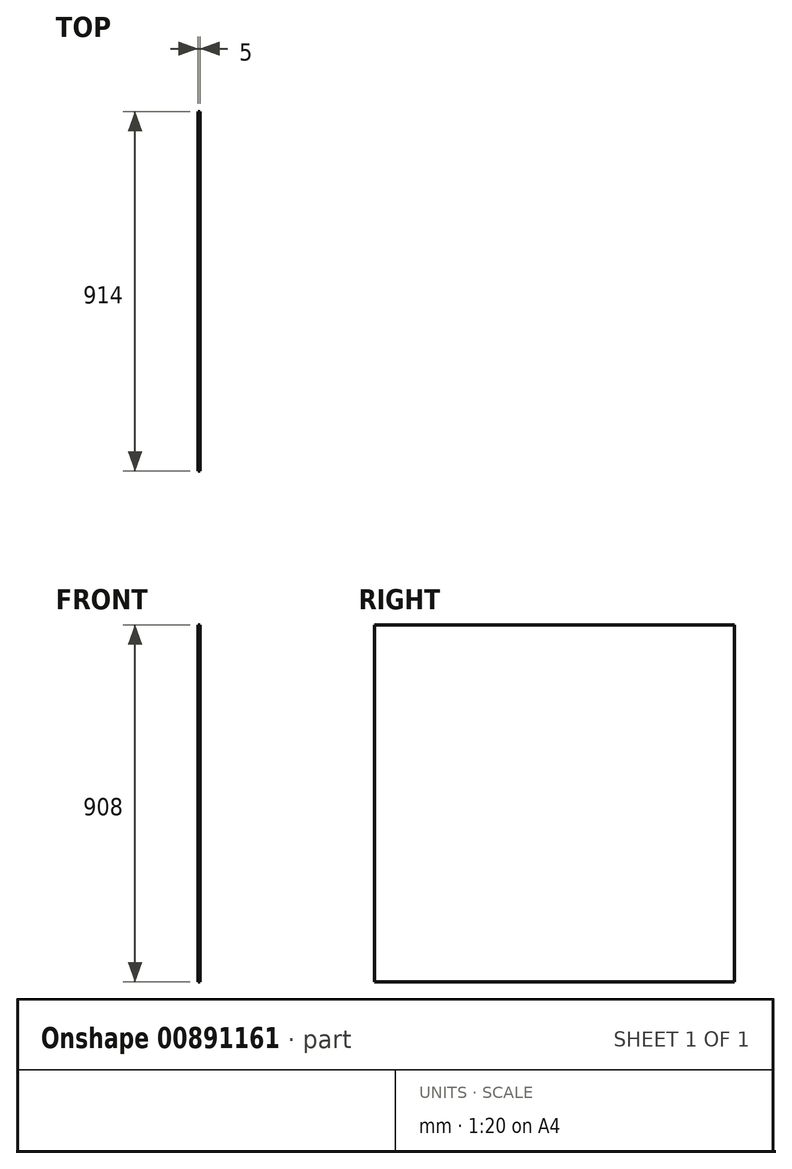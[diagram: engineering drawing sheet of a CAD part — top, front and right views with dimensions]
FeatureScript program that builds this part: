
annotation { "Feature Type Name" : "Feature", "Feature Type Description" : "" }
export const myFeature = defineFeature(function(context is Context, id is Id, definition is map)
    precondition{}
    {
        {
            var Q0;
            Q0=qCreatedBy(makeId("Right.planeOp"),FACE);
            var sketch = newSketch(context, id + "F0", { "sketchPlane" : qUnion([Q0])});
            skLineSegment(sketch, "E0.bottom", {"start": v(-454.54, 438.41) * mm, "end": v(459.46, 438.41) * mm});
            skLineSegment(sketch, "E0.top", {"start": v(-454.54, -469.59) * mm, "end": v(459.46, -469.59) * mm});
            skLineSegment(sketch, "E0.left", {"start": v(-454.54, 438.41) * mm, "end": v(-454.54, -469.59) * mm});
            skLineSegment(sketch, "E0.right", {"start": v(459.46, 438.41) * mm, "end": v(459.46, -469.59) * mm});
            skSolve(sketch);
        }
        {
            var Q0;
            Q0=makeQuery(id+"F0.imprint","IMPRINT",FACE,{"disambiguationData":[TD([[makeQuery(id+"F0.imprint","IMPRINT",EDGE,{"derivedFrom":sQuery(id+"F0.wireOp",EDGE,"E0.bottom")}),-1.0]])]});
            extrude(context, id + "F1", {"entities" : qUnion([Q0]), "depth" : 5 * mm, "offsetDistance" : 25 * mm});
        }
    });
